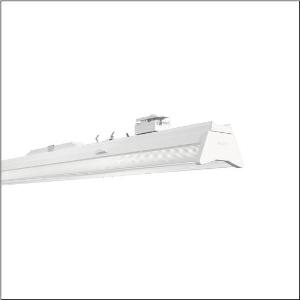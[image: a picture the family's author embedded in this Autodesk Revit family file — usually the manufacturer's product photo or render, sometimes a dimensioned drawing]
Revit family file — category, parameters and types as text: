
# Revit family: licross_r__21_performance_mo_52td16cn445g_c2c6
name_source: partatom
category: Lighting Fixtures
units: mm (PartAtom-declared; Revit-internal decimal feet)

## family parameters
Cut with Voids When Loaded = No
Host = Face
Light Source = No
Part Type = Normal
Room Calculation Point = No
Round Connector Dimension = Use Diameter
Shared = No

## types (1)
- --- (1 x LED, 4500 lm, 24.1 W, 4000K)
    Apparent Load = 24 VA
    CIE Flux Codes = 66 88 96 79 100
    Color Rendering = 80
    Color Temperature = 4000K
    Default Elevation = 1800 mm
    Description = Licross® 21 Performance MO, luminaire insert, of sheet steel, galvanised, coil coated, white, length: 1.500mm, width: 120mm, height: 123mm, LED rated luminous flux: 4.500lm, light colour: 840, control gear: ON/OFF Multilumen, CLOi, control gear: ECG Multilumen, with plug, 3-pole, with phase selection, mains connection: 220..240V, AC, 50/60Hz, start of lifetime: 24W, end of service life: 28W, halogen-free wiring, primary light control with lens, of plastic, primary optical cover: cover, of PMMA, CAT 2 (L<= 3000cd/m²), light emission: direct/indirect distribution, primary light characteristic: symmetric, protection rating (complete): IP54, insulation class (complete): insulation class I (protective earthing), certification: CE, ENEC, UKCA, protection symbol: D if used in an environment with non-conductive dust loads with corresponding accessories, impact resistance: IK06, permissible ambient temperature for indoor applications: -35..+55°C, corresponds to IFS (International Featured Standards) requirements for safety and quality in the food industry, reducing of maximum allowable ambient temperature of 5°C with ceiling mounting, LABS conformity tested according to VDMA 24364:2018-05, packaging unit: 1 piece
    Height = 114 mm
    Lamp = 1 x LED
    Lamp Light Flux = 4500 lm
    Lamp Power = 24.1 W
    Lamp count = 1
    Length = 1500 mm
    Luminous efficacy = 187 lm/W
    Manufacturer = Siteco
    ModVariant = No
    Model = 52TD16CN445G
    Mounting Place = Ceiling
    Mounting Type = Pendant
    Number of Poles = 1
    OnlyDefault = Yes
    Power Factor = 1
    Product Name = Licross® 21 Performance MO
    Product group = luminaire insert
    ProductGroupID = 901
    Protection Class = Protection class I
    Protection Degree = IP 54
    RLX_Detail_Level = 1
    RLX_Emergency_Light_Flux = 0 lm
    RLX_Emergency_Type = 0
    RLX_Emergency_Type_DB = No
    RlxData = <blob elided: 31377 chars, md5=9c040c54>
    Socket = socket
    Standby Power = 0 W
    System Light Flux = 4500 lm
    System Power = 24 W
    Type Comments = factory setting: luminous flux: 100 % | (A | C | E) | 55 mA
    Type Image = l_1256138.jpg
    URL = http://relux.com
    VarID = @adj_007003
    Voltage = 0 V
    Weight = 0.00 kg
    Width = 120 mm

## geometry (parser evidence)
native form markers: Blend x4, Sweep x10
no freeform markers — native parametric forms only
